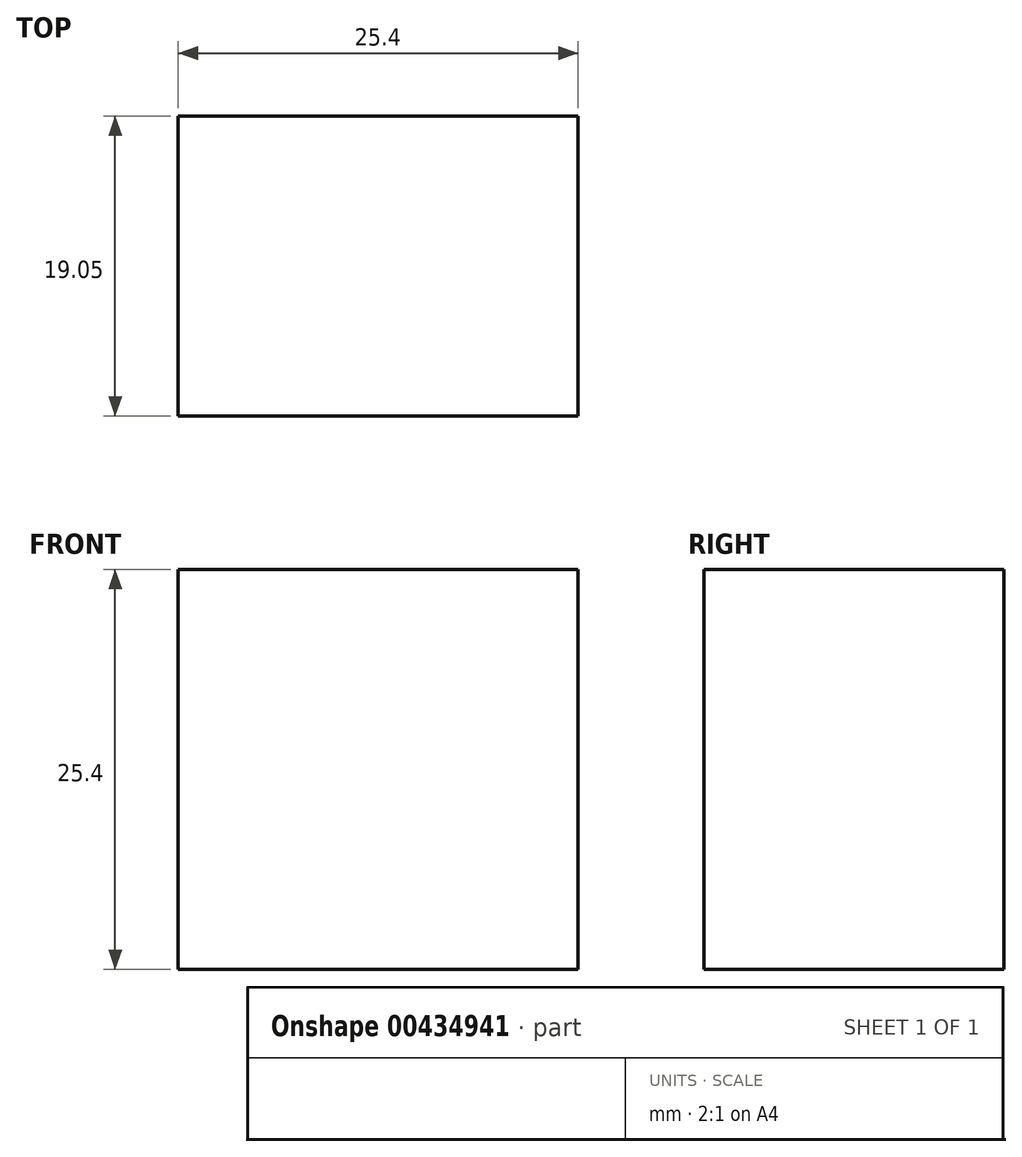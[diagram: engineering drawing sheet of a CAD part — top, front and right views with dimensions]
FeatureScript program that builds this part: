
annotation { "Feature Type Name" : "Feature", "Feature Type Description" : "" }
export const myFeature = defineFeature(function(context is Context, id is Id, definition is map)
    precondition{}
    {
        {
            var Q0;
            Q0=qCreatedBy(makeId("Front.planeOp"),FACE);
            var sketch = newSketch(context, id + "F0", { "sketchPlane" : qUnion([Q0])});
            skLineSegment(sketch, "E0", {"start": v(0, 0) * mm, "end": v(25.4, 0) * mm});
            skLineSegment(sketch, "E1", {"start": v(25.4, 0) * mm, "end": v(25.4, -25.4) * mm});
            skLineSegment(sketch, "E2", {"start": v(25.4, -25.4) * mm, "end": v(0, -25.4) * mm});
            skLineSegment(sketch, "E3", {"start": v(0, -25.4) * mm, "end": v(0, 0) * mm});
            skSolve(sketch);
        }
        {
            var Q0;
            Q0=makeQuery(id+"F0.imprint","IMPRINT",FACE,{"disambiguationData":[TD([[makeQuery(id+"F0.imprint","IMPRINT",EDGE,{"derivedFrom":sQuery(id+"F0.wireOp",EDGE,"E0")}),-1.0]])]});
            extrude(context, id + "F1", {"entities" : qUnion([Q0]), "depth" : 19.05 * mm});
        }
    });
